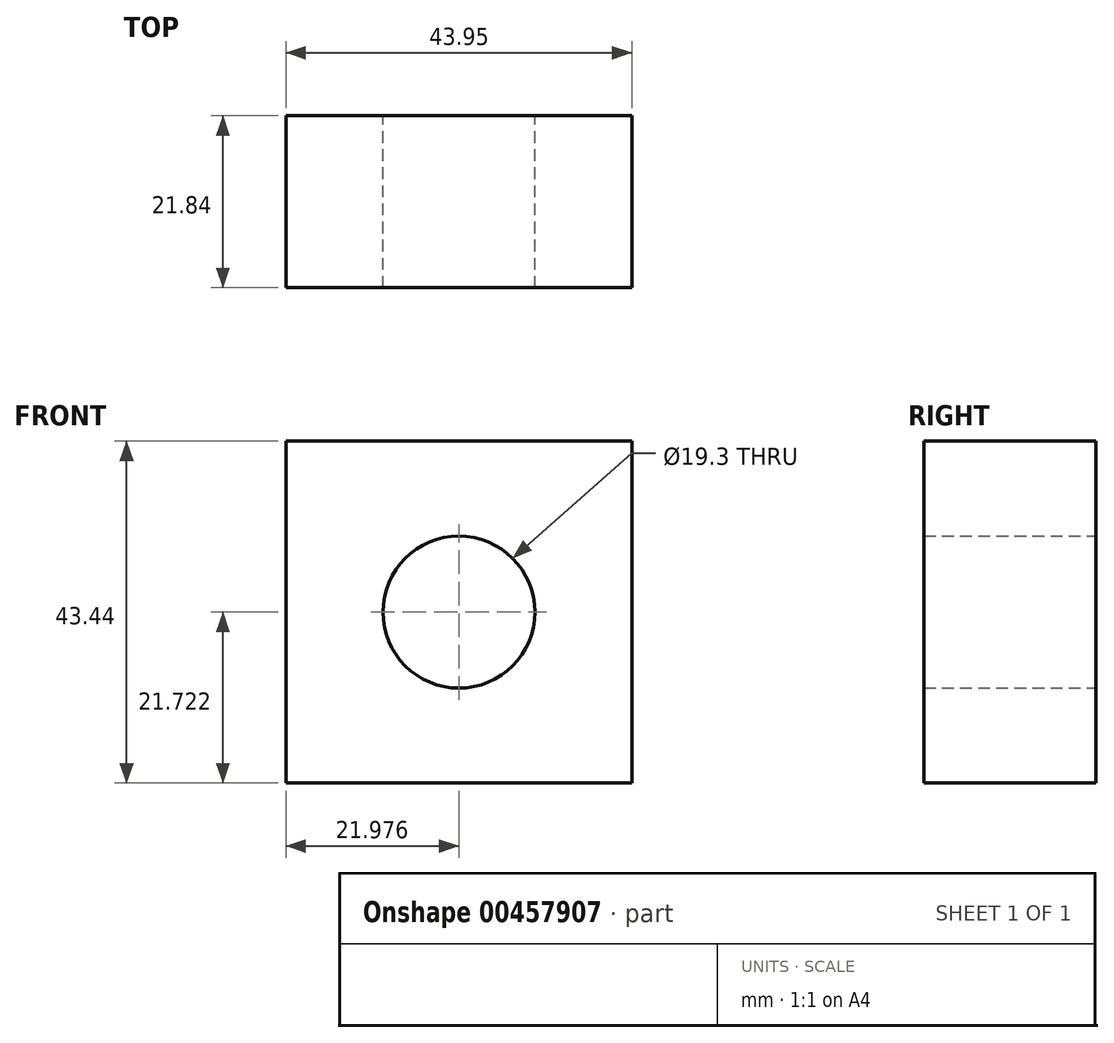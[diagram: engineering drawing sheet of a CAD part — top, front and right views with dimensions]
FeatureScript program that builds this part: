
annotation { "Feature Type Name" : "Feature", "Feature Type Description" : "" }
export const myFeature = defineFeature(function(context is Context, id is Id, definition is map)
    precondition{}
    {
        {
            var Q0;
            Q0=qCreatedBy(makeId("Front.planeOp"),FACE);
            var sketch = newSketch(context, id + "F0", { "sketchPlane" : qUnion([Q0])});
            skLineSegment(sketch, "E0.bottom", {"start": v(-48.2, 51.03) * mm, "end": v(-4.26, 51.03) * mm});
            skLineSegment(sketch, "E0.top", {"start": v(-48.2, 7.6) * mm, "end": v(-4.26, 7.6) * mm});
            skLineSegment(sketch, "E0.left", {"start": v(-48.2, 51.03) * mm, "end": v(-48.2, 7.6) * mm});
            skLineSegment(sketch, "E0.right", {"start": v(-4.26, 51.03) * mm, "end": v(-4.26, 7.6) * mm});
            skLineSegment(sketch, "E1", {"start": v(-26.23, 51.03) * mm, "end": v(-26.23, 7.6) * mm, "construction": true});
            skLineSegment(sketch, "E2", {"start": v(-48.2, 29.31) * mm, "end": v(-4.26, 29.31) * mm, "construction": true});
            skCircle(sketch, "E3", {"center": v(-26.23, 29.31) * mm, "radius": 9.65 * mm});
            skSolve(sketch);
        }
        {
            var Q0;
            Q0 = qSketchRegion(id + "F0", true);
            extrude(context, id + "F1", {"entities" : qUnion([Q0]), "depth" : 21.84 * mm});
        }
    });
